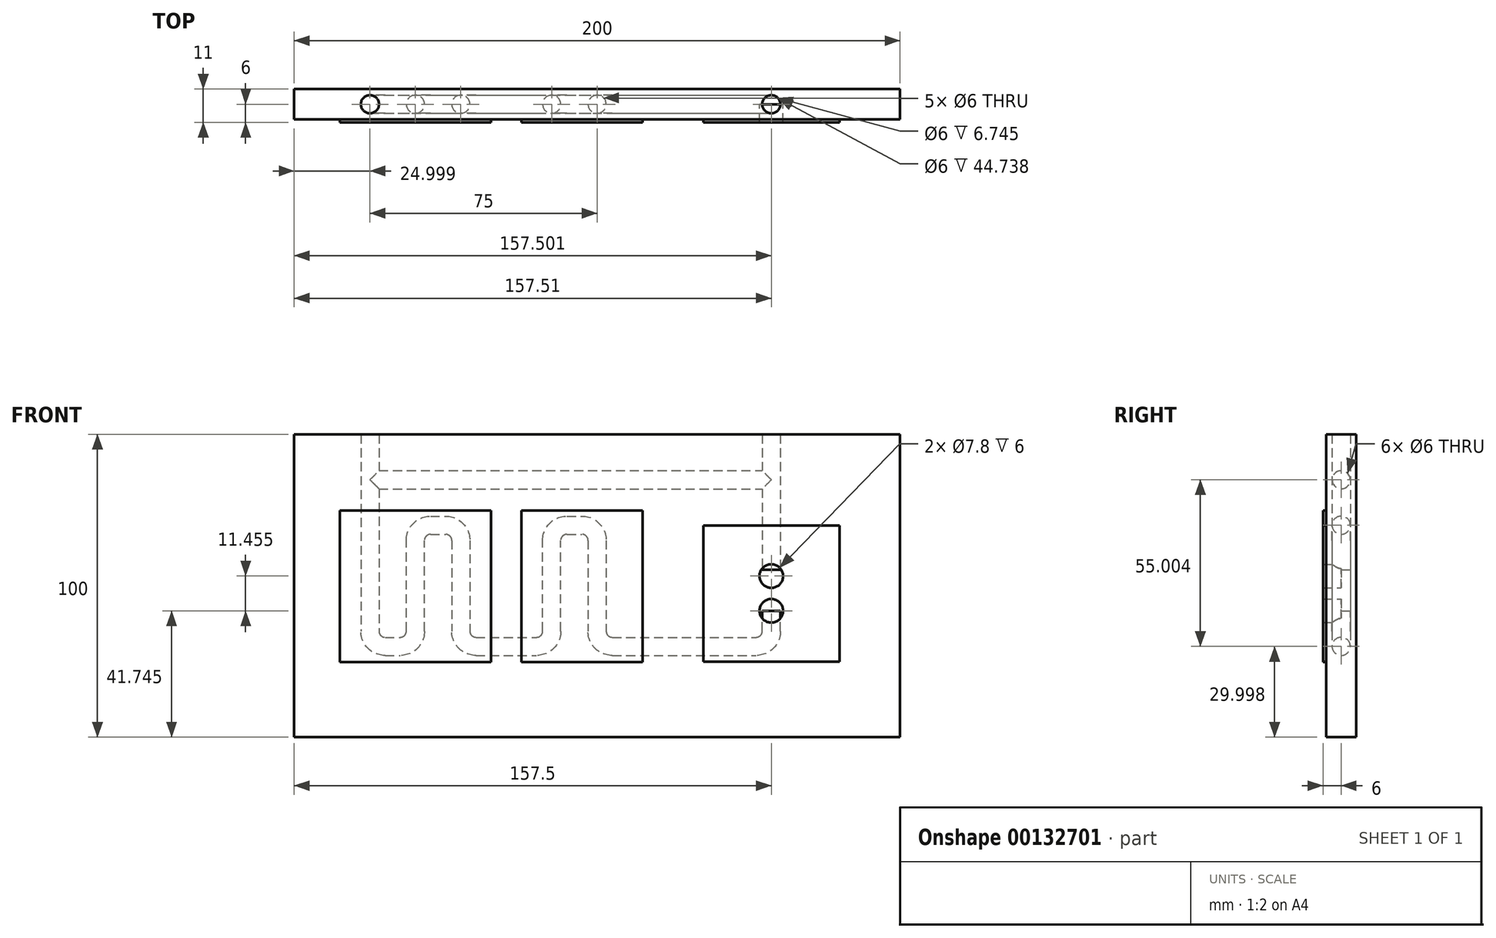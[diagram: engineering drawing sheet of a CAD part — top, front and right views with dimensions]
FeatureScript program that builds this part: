
annotation { "Feature Type Name" : "Feature", "Feature Type Description" : "" }
export const myFeature = defineFeature(function(context is Context, id is Id, definition is map)
    precondition{}
    {
        {
            var Q0;
            Q0=qCreatedBy(makeId("Front.planeOp"),FACE);
            var sketch = newSketch(context, id + "F0", { "sketchPlane" : qUnion([Q0])});
            skLineSegment(sketch, "E0.bottom", {"start": v(100, 50) * mm, "end": v(-100, 50) * mm});
            skLineSegment(sketch, "E0.top", {"start": v(100, -50) * mm, "end": v(-100, -50) * mm});
            skLineSegment(sketch, "E0.left", {"start": v(100, 50) * mm, "end": v(100, -50) * mm});
            skLineSegment(sketch, "E0.right", {"start": v(-100, 50) * mm, "end": v(-100, -50) * mm});
            skPoint(sketch, "E0.middle", {"position": v(0, 0) * mm});
            skLineSegment(sketch, "E1.bottom", {"start": v(90, 40) * mm, "end": v(-90, 40) * mm});
            skLineSegment(sketch, "E1.top", {"start": v(90, -40) * mm, "end": v(-90, -40) * mm});
            skLineSegment(sketch, "E1.left", {"start": v(90, 40) * mm, "end": v(90, -40) * mm});
            skLineSegment(sketch, "E1.right", {"start": v(-90, 40) * mm, "end": v(-90, -40) * mm});
            skLineSegment(sketch, "E2.bottom", {"start": v(35, 20) * mm, "end": v(80, 20) * mm});
            skLineSegment(sketch, "E2.top", {"start": v(35, -25) * mm, "end": v(80, -25) * mm});
            skLineSegment(sketch, "E2.left", {"start": v(35, 20) * mm, "end": v(35, -25) * mm});
            skLineSegment(sketch, "E2.right", {"start": v(80, 20) * mm, "end": v(80, -25) * mm});
            skLineSegment(sketch, "E3", {"start": v(-75, 63.41) * mm, "end": v(-75, 40) * mm});
            skLineSegment(sketch, "E4", {"start": v(-60, -15) * mm, "end": v(-60, 15) * mm});
            skLineSegment(sketch, "E5.top", {"start": v(-85, -25) * mm, "end": v(-35, -25) * mm});
            skLineSegment(sketch, "E5.right", {"start": v(-35, 25) * mm, "end": v(-35, -25) * mm});
            skLineSegment(sketch, "E6", {"start": v(-85, -25) * mm, "end": v(-85, 25) * mm});
            skLineSegment(sketch, "E7", {"start": v(-85, 25) * mm, "end": v(-35, 25) * mm});
            skLineSegment(sketch, "E8", {"start": v(-75, 40) * mm, "end": v(-75, -15) * mm});
            skLineSegment(sketch, "E9", {"start": v(-70, -20) * mm, "end": v(-65, -20) * mm});
            skPoint(sketch, "E10.visualSharp", {"position": v(-75, -20) * mm});
            skArc(sketch, "E10.filletArc", {"start": v(-75, -15) * mm, "mid": v(-73.54, -18.54) * mm, "end": v(-70, -20) * mm});
            skPoint(sketch, "E11.visualSharp", {"position": v(-60, -20) * mm});
            skArc(sketch, "E11.filletArc", {"start": v(-65, -20) * mm, "mid": v(-61.46, -18.54) * mm, "end": v(-60, -15) * mm});
            skPoint(sketch, "E12.visualSharp", {"position": v(-60, 20) * mm});
            skArc(sketch, "E12.filletArc", {"start": v(-55, 20) * mm, "mid": v(-58.54, 18.54) * mm, "end": v(-60, 15) * mm});
            skPoint(sketch, "E13.visualSharp", {"position": v(-45, 20) * mm});
            skArc(sketch, "E13.filletArc", {"start": v(-45, 15) * mm, "mid": v(-46.46, 18.54) * mm, "end": v(-50, 20) * mm});
            skLineSegment(sketch, "E14.bottom", {"start": v(-25, 25) * mm, "end": v(15, 25) * mm});
            skLineSegment(sketch, "E14.top", {"start": v(-25, -25) * mm, "end": v(15, -25) * mm});
            skLineSegment(sketch, "E14.left", {"start": v(-25, 25) * mm, "end": v(-25, -25) * mm});
            skLineSegment(sketch, "E14.right", {"start": v(15, 25) * mm, "end": v(15, -25) * mm});
            skLineSegment(sketch, "E15", {"start": v(57.5, 35) * mm, "end": v(-75, 35) * mm});
            skLineSegment(sketch, "E16", {"start": v(-55, 20) * mm, "end": v(-50, 20) * mm});
            skLineSegment(sketch, "E17", {"start": v(-45, 15) * mm, "end": v(-45, -15) * mm});
            skPoint(sketch, "E18.visualSharp", {"position": v(-45, -20) * mm});
            skArc(sketch, "E18.filletArc", {"start": v(-45, -15) * mm, "mid": v(-43.54, -18.54) * mm, "end": v(-40, -20) * mm});
            skLineSegment(sketch, "E19", {"start": v(-40, -20) * mm, "end": v(-20, -20) * mm});
            skPoint(sketch, "E20.visualSharp", {"position": v(-20, -20) * mm});
            skArc(sketch, "E20.filletArc", {"start": v(-20, -20) * mm, "mid": v(-16.46, -18.54) * mm, "end": v(-15, -15) * mm});
            skLineSegment(sketch, "E21", {"start": v(-15, 15) * mm, "end": v(-15, -15) * mm});
            skLineSegment(sketch, "E22", {"start": v(-10, 20) * mm, "end": v(-5, 20) * mm});
            skLineSegment(sketch, "E23", {"start": v(-15, 15) * mm, "end": v(-15, 15) * mm});
            skLineSegment(sketch, "E24", {"start": v(-10, 20) * mm, "end": v(-10, 20) * mm});
            skPoint(sketch, "E25.visualSharp", {"position": v(-15, 20) * mm});
            skArc(sketch, "E25.filletArc", {"start": v(-10, 20) * mm, "mid": v(-13.54, 18.54) * mm, "end": v(-15, 15) * mm});
            skLineSegment(sketch, "E26", {"start": v(-5, 20) * mm, "end": v(-5, 20) * mm});
            skLineSegment(sketch, "E27", {"start": v(0, 15) * mm, "end": v(0, -15) * mm});
            skPoint(sketch, "E28.visualSharp", {"position": v(0, 20) * mm});
            skArc(sketch, "E28.filletArc", {"start": v(0, 15) * mm, "mid": v(-1.46, 18.54) * mm, "end": v(-5, 20) * mm});
            skLineSegment(sketch, "E29", {"start": v(0, -15) * mm, "end": v(0, -15) * mm});
            skLineSegment(sketch, "E30", {"start": v(5, -20) * mm, "end": v(51.64, -20) * mm});
            skPoint(sketch, "E31.visualSharp", {"position": v(0, -20) * mm});
            skArc(sketch, "E31.filletArc", {"start": v(0, -15) * mm, "mid": v(1.46, -18.54) * mm, "end": v(5, -20) * mm});
            skCircle(sketch, "E32", {"center": v(57.5, 3.2) * mm, "radius": 3.9 * mm});
            skCircle(sketch, "E33", {"center": v(57.5, -8.26) * mm, "radius": 3.9 * mm});
            skLineSegment(sketch, "E34", {"start": v(51.64, -20) * mm, "end": v(52.5, -20) * mm});
            skLineSegment(sketch, "E35", {"start": v(57.5, -15) * mm, "end": v(57.5, -8.26) * mm});
            skPoint(sketch, "E36.visualSharp", {"position": v(57.5, -20) * mm});
            skArc(sketch, "E36.filletArc", {"start": v(52.5, -20) * mm, "mid": v(56.04, -18.54) * mm, "end": v(57.5, -15) * mm});
            skLineSegment(sketch, "E37", {"start": v(57.5, 3.2) * mm, "end": v(57.5, 61.35) * mm});
            skSolve(sketch);
        }
        {
            var Q0;
            Q0=qCreatedBy(makeId("Top.planeOp"),FACE);
            var Q1;
            Q1=sQuery(id+"F0.wireOp",VERTEX,"E3.start");
            cPlane(context, id + "F1", {"entities" : qUnion([Q0, Q1]), "cplaneType" : CPlaneType.PLANE_POINT, "offset" : 25 * mm, "width" : 150 * mm, "height" : 150 * mm});
        }
        {
            var Q0;
            Q0=qCreatedBy(id+"F1.planeOp",FACE);
            var sketch = newSketch(context, id + "F2", { "sketchPlane" : qUnion([Q0])});
            skCircle(sketch, "E38", {"center": v(-75, 0) * mm, "radius": 3 * mm});
            skCircle(sketch, "E39", {"center": v(57.51, 0) * mm, "radius": 3 * mm});
            skSolve(sketch);
        }
        {
            var Q0;
            {var subQ4=sQuery(id+"F0.wireOp",EDGE,"E0.right");Q0=makeQuery(id+"F0.imprint","IMPRINT",FACE,{"disambiguationData":[TD([[makeQuery(id+"F0.imprint","IMPRINT",EDGE,{"derivedFrom":subQ4}),1.0]])]});}
            var Q1;
            {var subQ4=sQuery(id+"F0.wireOp",EDGE,"E0.left");Q1=makeQuery(id+"F0.imprint","IMPRINT",FACE,{"disambiguationData":[TD([[makeQuery(id+"F0.imprint","IMPRINT",EDGE,{"derivedFrom":subQ4}),-1.0]])]});}
            var Q2;
            {var subQ18=sQuery(id+"F0.wireOp",EDGE,"E1.right");Q2=makeQuery(id+"F0.imprint","IMPRINT",FACE,{"disambiguationData":[TD([[makeQuery(id+"F0.imprint","IMPRINT",EDGE,{"derivedFrom":subQ18}),1.0]])]});}
            var Q3;
            {var subQ11=sQuery(id+"F0.wireOp",EDGE,"E1.left");Q3=makeQuery(id+"F0.imprint","IMPRINT",FACE,{"disambiguationData":[TD([[makeQuery(id+"F0.imprint","IMPRINT",EDGE,{"derivedFrom":subQ11}),-1.0]])]});}
            var Q4;
            {var subQ5=sQuery(id+"F0.wireOp",EDGE,"E2.right");Q4=makeQuery(id+"F0.imprint","IMPRINT",FACE,{"disambiguationData":[TD([[makeQuery(id+"F0.imprint","IMPRINT",EDGE,{"derivedFrom":subQ5}),-1.0]])]});}
            var Q5;
            {var subQ1=sQuery(id+"F0.wireOp",EDGE,"E2.left");var subQ5=sQuery(id+"F0.wireOp",EDGE,"E2.top");var subQ6=makeQuery(id+"F0.imprint","INTERSECT",VERTEX,{"derivedFrom":[subQ5,subQ1]});Q5=makeQuery(id+"F0.imprint","IMPRINT",FACE,{"disambiguationData":[TD([[makeQuery(id+"F0.imprint","IMPRINT",EDGE,{"disambiguationData":[TD([[subQ6,-1.0]])],"derivedFrom":subQ5}),1.0]])]});}
            var Q6;
            Q6=makeQuery(id+"F0.imprint","IMPRINT",FACE,{"disambiguationData":[TD([[makeQuery(id+"F0.imprint","IMPRINT",EDGE,{"derivedFrom":sQuery(id+"F0.wireOp",EDGE,"6O3oJnMi-3r5Y-Mh4t-gewl-6Bgbzzf1IErF")}),-1.0]])]});
            var Q7;
            Q7=makeQuery(id+"F0.imprint","IMPRINT",FACE,{"disambiguationData":[TD([[makeQuery(id+"F0.imprint","IMPRINT",EDGE,{"derivedFrom":sQuery(id+"F0.wireOp",EDGE,"6O3oJnMi-3r5Y-Mh4t-gewl-6Bgbzzf1IErF")}),1.0]])]});
            var Q8;
            Q8=makeQuery(id+"F0.imprint","IMPRINT",FACE,{"disambiguationData":[TD([[makeQuery(id+"F0.imprint","IMPRINT",EDGE,{"derivedFrom":sQuery(id+"F0.wireOp",EDGE,"E4")}),1.0]])]});
            var Q9;
            Q9=makeQuery(id+"F0.imprint","IMPRINT",FACE,{"disambiguationData":[TD([[makeQuery(id+"F0.imprint","IMPRINT",EDGE,{"derivedFrom":sQuery(id+"F0.wireOp",EDGE,"E4")}),-1.0]])]});
            var Q10;
            {var subQ14=sQuery(id+"F0.wireOp",EDGE,"E2.left");Q10=makeQuery(id+"F0.imprint","IMPRINT",FACE,{"disambiguationData":[TD([[makeQuery(id+"F0.imprint","IMPRINT",EDGE,{"derivedFrom":subQ14}),-1.0]])]});}
            var Q11;
            {var subQ9=sQuery(id+"F0.wireOp",EDGE,"E14.bottom");Q11=makeQuery(id+"F0.imprint","IMPRINT",FACE,{"disambiguationData":[TD([[makeQuery(id+"F0.imprint","IMPRINT",EDGE,{"derivedFrom":subQ9}),-1.0]])]});}
            var Q12;
            {var subQ0=sQuery(id+"F0.wireOp",EDGE,"h2m8kfxB-LdNM-kv8t-3MnA-ep9ZYku23Ott");Q12=makeQuery(id+"F0.imprint","IMPRINT",FACE,{"disambiguationData":[TD([[makeQuery(id+"F0.imprint","IMPRINT",EDGE,{"derivedFrom":subQ0}),-1.0]])]});}
            var Q13;
            {var subQ0=sQuery(id+"F0.wireOp",EDGE,"53eGvYAs-UcRD-kFIF-hqhq-a7OkAW00z16i");var subQ1=sQuery(id+"F0.wireOp",EDGE,"E0.bottom");var subQ2=makeQuery(id+"F0.imprint","INTERSECT",VERTEX,{"derivedFrom":[subQ1,subQ0]});Q13=makeQuery(id+"F0.imprint","IMPRINT",FACE,{"disambiguationData":[TD([[makeQuery(id+"F0.imprint","IMPRINT",EDGE,{"disambiguationData":[TD([[subQ2,-1.0]])],"derivedFrom":subQ1}),1.0]])]});}
            var Q14;
            {var subQ1=sQuery(id+"F0.wireOp",EDGE,"E15");Q14=makeQuery(id+"F0.imprint","IMPRINT",FACE,{"disambiguationData":[TD([[makeQuery(id+"F0.imprint","IMPRINT",EDGE,{"derivedFrom":subQ1}),-1.0]])]});}
            var Q15;
            {var subQ0=sQuery(id+"F0.wireOp",EDGE,"E14.top");Q15=makeQuery(id+"F0.imprint","IMPRINT",FACE,{"disambiguationData":[TD([[makeQuery(id+"F0.imprint","IMPRINT",EDGE,{"derivedFrom":subQ0}),1.0]])]});}
            var Q16;
            Q16=makeQuery(id+"F0.imprint","IMPRINT",FACE,{"disambiguationData":[TD([[makeQuery(id+"F0.imprint","IMPRINT",EDGE,{"derivedFrom":sQuery(id+"F0.wireOp",EDGE,"E32")}),1.0]])]});
            var Q17;
            Q17=makeQuery(id+"F0.imprint","IMPRINT",FACE,{"disambiguationData":[TD([[makeQuery(id+"F0.imprint","IMPRINT",EDGE,{"derivedFrom":sQuery(id+"F0.wireOp",EDGE,"E33")}),1.0]])]});
            var Q18;
            {var subQ0=sQuery(id+"F0.wireOp",EDGE,"E37");var subQ1=sQuery(id+"F0.wireOp",EDGE,"E0.bottom");var subQ2=makeQuery(id+"F0.imprint","INTERSECT",VERTEX,{"derivedFrom":[subQ1,subQ0]});Q18=makeQuery(id+"F0.imprint","IMPRINT",FACE,{"disambiguationData":[TD([[makeQuery(id+"F0.imprint","IMPRINT",EDGE,{"disambiguationData":[TD([[subQ2,-1.0]])],"derivedFrom":subQ1}),1.0]])]});}
            extrude(context, id + "F3", {"entities" : qUnion([Q0, Q1, Q2, Q3, Q4, Q5, Q6, Q7, Q8, Q9, Q10, Q11, Q12, Q13, Q14, Q15, Q16, Q17, Q18]), "endBound" : BoundingType.SYMMETRIC, "depth" : 10 * mm});
        }
        {
            var Q0;
            Q0=qCreatedBy(makeId("Right.planeOp"),FACE);
            var Q1;
            Q1=sQuery(id+"F0.wireOp",VERTEX,"E15.end");
            cPlane(context, id + "F4", {"entities" : qUnion([Q0, Q1]), "cplaneType" : CPlaneType.PLANE_POINT, "offset" : 25 * mm, "width" : 150 * mm, "height" : 150 * mm});
        }
        {
            var Q0;
            Q0=qCreatedBy(id+"F4.planeOp",FACE);
            var sketch = newSketch(context, id + "F5", { "sketchPlane" : qUnion([Q0])});
            skCircle(sketch, "E40", {"center": v(0, 35) * mm, "radius": 3 * mm});
            skSolve(sketch);
        }
        {
            var Q0;
            Q0 = qSketchRegion(id + "F5", true);
            var Q1;
            Q1=sQuery(id+"F0.wireOp",EDGE,"E15");
            var Q2;
            Q2=sQuery(id+"F0.wireOp",EDGE,"7Qz8wZhT-pwLB-z1eM-rq2P-8lw9gPCXK3l3");
            sweep(context, id + "F6", {"operationType" : NewBodyOperationType.REMOVE, "profiles" : qUnion([Q0]), "path" : qUnion([Q1, Q2])});
        }
        {
            var Q0;
            Q0=makeQuery(id+"F3.opExtrude","CAP_FACE",FACE,{"disambiguationData":[OSD([sQuery(id+"F0.wireOp",EDGE,"E0.bottom"),sQuery(id+"F0.wireOp",EDGE,"E0.top"),sQuery(id+"F0.wireOp",EDGE,"E0.left"),sQuery(id+"F0.wireOp",EDGE,"E0.right")])],"isStart":false});
            var sketch = newSketch(context, id + "F7", { "sketchPlane" : qUnion([Q0])});
            skLineSegment(sketch, "E41.bottom", {"start": v(-85, 24.81) * mm, "end": v(-35, 24.81) * mm});
            skLineSegment(sketch, "E41.top", {"start": v(-85, -25.19) * mm, "end": v(-35, -25.19) * mm});
            skLineSegment(sketch, "E41.left", {"start": v(-85, 24.81) * mm, "end": v(-85, -25.19) * mm});
            skLineSegment(sketch, "E41.right", {"start": v(-35, 24.81) * mm, "end": v(-35, -25.19) * mm});
            skLineSegment(sketch, "E42.bottom", {"start": v(-25.03, 24.81) * mm, "end": v(14.97, 24.81) * mm});
            skLineSegment(sketch, "E42.top", {"start": v(-25.03, -25.19) * mm, "end": v(14.97, -25.19) * mm});
            skLineSegment(sketch, "E42.left", {"start": v(-25.03, 24.81) * mm, "end": v(-25.03, -25.19) * mm});
            skLineSegment(sketch, "E42.right", {"start": v(14.97, 24.81) * mm, "end": v(14.97, -25.19) * mm});
            skLineSegment(sketch, "E43.bottom", {"start": v(35.06, 19.96) * mm, "end": v(80.06, 19.96) * mm});
            skLineSegment(sketch, "E43.top", {"start": v(35.06, -25.04) * mm, "end": v(80.06, -25.04) * mm});
            skLineSegment(sketch, "E43.left", {"start": v(35.06, 19.96) * mm, "end": v(35.06, -25.04) * mm});
            skLineSegment(sketch, "E43.right", {"start": v(80.06, 19.96) * mm, "end": v(80.06, -25.04) * mm});
            skSolve(sketch);
        }
        {
            var Q0;
            Q0 = qSketchRegion(id + "F7", true);
            extrude(context, id + "F8", {"entities" : qUnion([Q0]), "operationType" : NewBodyOperationType.ADD, "depth" : 1 * mm});
        }
        {
            var Q0;
            Q0=makeQuery(id+"F2.imprint","IMPRINT",FACE,{"disambiguationData":[TD([[makeQuery(id+"F2.imprint","IMPRINT",EDGE,{"derivedFrom":sQuery(id+"F2.wireOp",EDGE,"E38")}),1.0]])]});
            var Q1;
            Q1=sQuery(id+"F0.wireOp",EDGE,"E3");
            var Q2;
            Q2=sQuery(id+"F0.wireOp",EDGE,"E8");
            var Q3;
            Q3=sQuery(id+"F0.wireOp",EDGE,"E10.filletArc");
            var Q4;
            Q4=sQuery(id+"F0.wireOp",EDGE,"E9");
            var Q5;
            Q5=sQuery(id+"F0.wireOp",EDGE,"E11.filletArc");
            var Q6;
            Q6=sQuery(id+"F0.wireOp",EDGE,"E4");
            var Q7;
            Q7=sQuery(id+"F0.wireOp",EDGE,"E12.filletArc");
            var Q8;
            Q8=sQuery(id+"F0.wireOp",EDGE,"E16");
            var Q9;
            Q9=sQuery(id+"F0.wireOp",EDGE,"E13.filletArc");
            var Q10;
            Q10=sQuery(id+"F0.wireOp",EDGE,"E17");
            var Q11;
            Q11=sQuery(id+"F0.wireOp",EDGE,"E18.filletArc");
            var Q12;
            Q12=sQuery(id+"F0.wireOp",EDGE,"E19");
            var Q13;
            Q13=sQuery(id+"F0.wireOp",EDGE,"E20.filletArc");
            var Q14;
            Q14=sQuery(id+"F0.wireOp",EDGE,"E21");
            var Q15;
            Q15=sQuery(id+"F0.wireOp",EDGE,"E25.filletArc");
            var Q16;
            Q16=sQuery(id+"F0.wireOp",EDGE,"E22");
            var Q17;
            Q17=sQuery(id+"F0.wireOp",EDGE,"E28.filletArc");
            var Q18;
            Q18=sQuery(id+"F0.wireOp",EDGE,"E27");
            var Q19;
            Q19=sQuery(id+"F0.wireOp",EDGE,"E31.filletArc");
            var Q20;
            Q20=sQuery(id+"F0.wireOp",EDGE,"E30");
            var Q21;
            Q21=sQuery(id+"F0.wireOp",EDGE,"E34");
            var Q22;
            Q22=sQuery(id+"F0.wireOp",EDGE,"E36.filletArc");
            var Q23;
            Q23=sQuery(id+"F0.wireOp",EDGE,"E35");
            sweep(context, id + "F9", {"operationType" : NewBodyOperationType.REMOVE, "profiles" : qUnion([Q0]), "path" : qUnion([Q1, Q2, Q3, Q4, Q5, Q6, Q7, Q8, Q9, Q10, Q11, Q12, Q13, Q14, Q15, Q16, Q17, Q18, Q19, Q20, Q21, Q22, Q23])});
        }
        {
            var Q0;
            Q0=makeQuery(id+"F0.imprint","IMPRINT",FACE,{"disambiguationData":[TD([[makeQuery(id+"F0.imprint","IMPRINT",EDGE,{"derivedFrom":sQuery(id+"F0.wireOp",EDGE,"E33")}),1.0]])]});
            var Q1;
            Q1=makeQuery(id+"F0.imprint","IMPRINT",FACE,{"disambiguationData":[TD([[makeQuery(id+"F0.imprint","IMPRINT",EDGE,{"derivedFrom":sQuery(id+"F0.wireOp",EDGE,"E32")}),1.0]])]});
            extrude(context, id + "F10", {"entities" : qUnion([Q0, Q1]), "operationType" : NewBodyOperationType.REMOVE, "endBound" : BoundingType.THROUGH_ALL, "depth" : 25 * mm});
        }
        {
            var Q0;
            Q0=makeQuery(id+"F2.imprint","IMPRINT",FACE,{"disambiguationData":[TD([[makeQuery(id+"F2.imprint","IMPRINT",EDGE,{"derivedFrom":sQuery(id+"F2.wireOp",EDGE,"E39")}),1.0]])]});
            var Q1;
            Q1=sQuery(id+"F0.wireOp",EDGE,"E37");
            sweep(context, id + "F11", {"operationType" : NewBodyOperationType.REMOVE, "profiles" : qUnion([Q0]), "path" : qUnion([Q1])});
        }
    });
